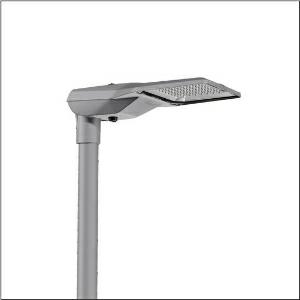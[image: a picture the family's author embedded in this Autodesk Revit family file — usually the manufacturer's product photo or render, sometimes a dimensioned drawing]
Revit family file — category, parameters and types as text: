
# Revit family: streetlight_sl_21_midi___p0_8ab_5xe3r33t08mb_ae32
name_source: partatom
category: Lighting Fixtures
units: mm (PartAtom-declared; Revit-internal decimal feet)

## family parameters
Cut with Voids When Loaded = No
Host = Face
Light Source = No
Part Type = Normal
Room Calculation Point = No
Round Connector Dimension = Use Diameter
Shared = No

## types (1)
- --- (1 x LED, 15870 lm, 136 W, 3000K)
    Apparent Load = 136 VA
    CIE Flux Codes = 36 71 98 100 100
    Color Rendering = 70
    Color Temperature = 3000K
    Default Elevation = 1800 mm
    Description = Streetlight SL 21 midi, mast luminaire, primary light control with lens, of PMMA, primary optical cover: cover, of toughened safety glass, transparent, light distribution: P0.8aB, light emission: direct distribution, primary light characteristic: asymmetric, installation type: post-top, side-entry, LED, High Power LED, rated luminous flux: 15.870lm, luminous efficacy: 117lm/W, light colour: 730, colour temperature: 3000K, control gear: D4i, control: pre-setting: logarithmic dimming characteristic, flexible luminous flux parameterisation, time-dependent luminous flux control, constant luminous flux control, overheat protection, mains connection: 230..240V, AC, 50/60Hz, start of lifetime: 136W, end of service life: 142W, reduction: 61W, luminaire housing, of diecast aluminium, powder-coated, Siteco® metallic grey (DB 702S), corrosivity category C5 mid according to DIN EN ISO 12944, multi-level sealing system, sealing non-destructively replaceable, inclination adjustable: 0°, 5°, 10°, 15°, please order mast flange separately, length: 644mm, width: 335mm, height: 110mm, mast flange for spigot size: 42mm (side-entry): 5XC10008XM4, 60/48mm (side-entry/post-top): 5XC10108XM2, 76/60mm (side-entry/post-top): 5XC10108XM1, mounting height: 4..8m, Smart Interface below and above, protection rating (complete): IP66, insulation class (complete): insulation class II (safety insulation), certification: CE, ENEC, ENEC+, VDE, impact resistance: IK10, permissible operating ambient temperature for outdoor applications: -40..+50°C, standard-compliant lighting for roads and squares, packaging unit: 1 piece

Light Distribution: P0.8aB
    Height = 111 mm
    Lamp = 1 x LED
    Lamp Light Flux = 15870 lm
    Lamp Power = 136 W
    Lamp count = 1
    Length = 644 mm
    Luminous efficacy = 117 lm/W
    Manufacturer = Siteco
    ModVariant = No
    Model = 5XE3R33T08MB
    Number of Poles = 1
    OnlyDefault = Yes
    Power Factor = 1
    Product Name = Streetlight SL 21 midi | P0.8aB
    Product group = mast luminaire | pylon top
    ProductGroupID = 6100
    Protection Class = Protection class II
    Protection Degree = IP 66
    RLX_Detail_Level = 1
    RLX_Emergency_Light_Flux = 0 lm
    RLX_Emergency_Type = 0
    RLX_Emergency_Type_DB = No
    RlxData = <blob elided: 90665 chars, md5=f5e16727>
    Socket = socket
    Standby Power = 0 W
    System Light Flux = 15870 lm
    System Power = 136 W
    Type Comments = factory setting: luminous flux: 100 % | dim-lin: 254 | 695 mA
    Type Image = l_1004304.jpg
    URL = http://relux.com
    VarID = @adj_096491
    Voltage = 0 V
    Weight = 0.00 kg
    Width = 336 mm

## geometry (parser evidence)
native form markers: Blend x4, Sweep x12
no freeform markers — native parametric forms only
